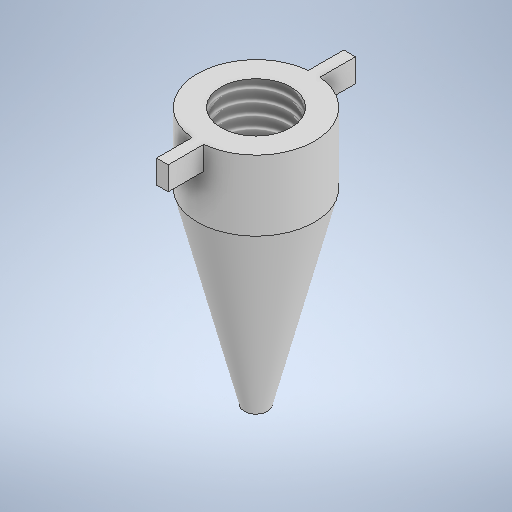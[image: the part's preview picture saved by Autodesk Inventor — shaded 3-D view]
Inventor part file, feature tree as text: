
AUTODESK INVENTOR PART (.ipt)
format: ipt  version: 2025.2 (Build 292293000, 293)  size: 279,552 bytes
history: native  units: mm
features: sketch x1, revolve x1, extrude x1, thread x1
ambient origin geometry x8: Origin, YZ Plane, XZ Plane, XY Plane, X Axis, Y Axis, Z Axis, Center Point
bodies: Solid1 (feature_tree)
feature tree (4):
  sketch  "Sketch1"  dims[d0=1.5mm d1=2.5mm d2=11.0mm d3=0.5mm d4=8.0mm d5=1.0mm d6=1.0mm d7=1.0mm d8=4.0mm d9=1.0mm d10=2.5mm d11=0.1mm d12=90.0deg d13=0.5mm d14=0.0mm d15=3.5mm d16=0.0mm]
  revolve  "Revolution1"  [1 undecoded]
  extrude  "Extrusion1"  Depth=11.0mm
  thread  "Thread1"  [1 undecoded]
note: 2 required parameter values undecoded (feature->parameter linkage not recoverable at this tier; creation-order binding heuristic only, values carry confidence <= 0.55)